# Revit family: FU_Modular_Sandler_Ari 1310
name_source: partatom
category: Furniture
units: mm (PartAtom-declared; Revit-internal decimal feet)

## family parameters
Always vertical = Yes
Cut with Voids When Loaded = No
OmniClass Number = 23.40.20.00
OmniClass Title = General Furniture and Specialties
Room Calculation Point = No
Shared = No
Work Plane-Based = No

## types (1)
- Ari 1310
    Default Elevation = 0 mm  [stored 0 ft]
    Depth = 780 mm  [stored 2.55906 ft]
    Description = Upholstered element without armrests in the Ari indoor modular seating range. Features an slender steel frame that forms an elegant double backrest support.
    Height = 780 mm  [stored 2.55906 ft]
    Manufacturer = Sandler
    Model = Ari 1310
    URL = https://www.sandlerseating.com
    Width = 720 mm  [stored 2.3622 ft]

note: [stored X ft] marks values corroborated as IEEE doubles in the binary element streams (Revit-internal decimal feet)

## geometry (parser evidence)
native form markers: Sweep x6
no freeform markers — native parametric forms only
